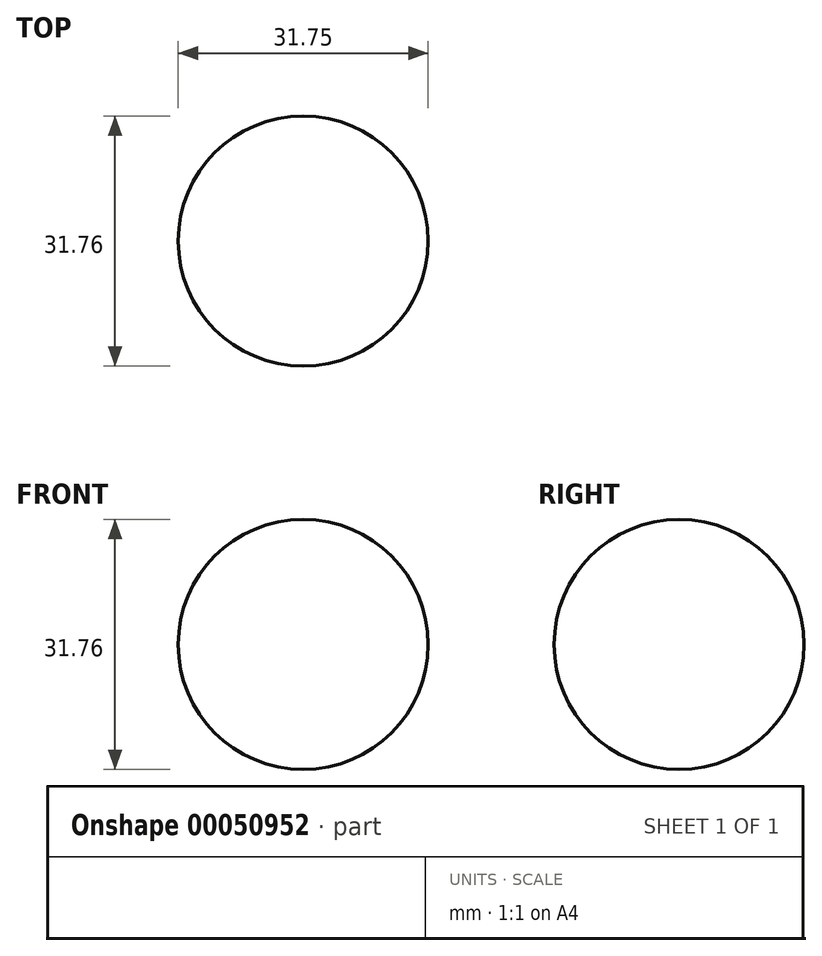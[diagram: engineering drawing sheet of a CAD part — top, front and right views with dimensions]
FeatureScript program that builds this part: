
annotation { "Feature Type Name" : "Feature", "Feature Type Description" : "" }
export const myFeature = defineFeature(function(context is Context, id is Id, definition is map)
    precondition{}
    {
        {
            var Q0;
            Q0=qCreatedBy(makeId("Top.planeOp"),FACE);
            var sketch = newSketch(context, id + "F0", { "sketchPlane" : qUnion([Q0])});
            skArc(sketch, "E0", {"start": v(0, 15.88) * mm, "mid": v(-15.88, 0) * mm, "end": v(0, -15.88) * mm});
            skLineSegment(sketch, "E1", {"start": v(0, -15.87) * mm, "end": v(0, 15.87) * mm});
            skSolve(sketch);
        }
        {
            var Q0;
            Q0=makeQuery(id+"F0.imprint","IMPRINT",FACE,{"disambiguationData":[TD([[makeQuery(id+"F0.imprint","IMPRINT",EDGE,{"derivedFrom":sQuery(id+"F0.wireOp",EDGE,"E0")}),1.0]])]});
            var Q1;
            Q1=sQuery(id+"F0.wireOp",EDGE,"E1");
            revolve(context, id + "F1", {"entities" : qUnion([Q0]), "axis" : qUnion([Q1]), "revolveType" : RevolveType.FULL});
        }
        {
            var Q0;
            Q0=qCreatedBy(makeId("Front.planeOp"),FACE);
            var sketch = newSketch(context, id + "F2", { "sketchPlane" : qUnion([Q0])});
            skCircle(sketch, "E2", {"center": v(4.95, 7.8) * mm, "radius": 3.15 * mm});
            skSolve(sketch);
        }
        {
            var Q0;
            Q0=sQuery(id+"F2.wireOp",EDGE,"E2");
            extrude(context, id + "F3", {"bodyType" : ToolBodyType.SURFACE, "surfaceEntities" : qUnion([Q0]), "depth" : 19.05 * mm});
        }
    });
